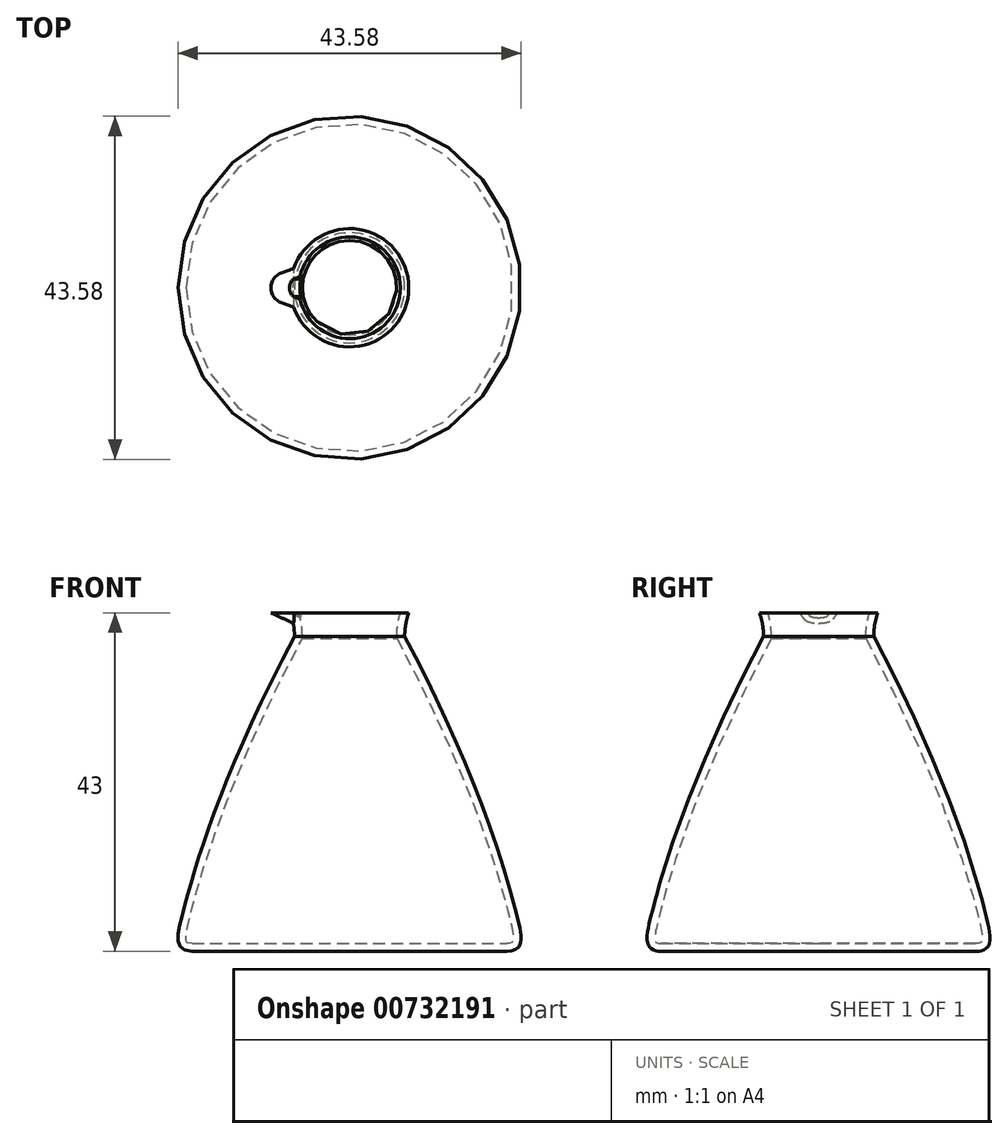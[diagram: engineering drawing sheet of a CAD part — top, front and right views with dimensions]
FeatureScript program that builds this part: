
annotation { "Feature Type Name" : "Feature", "Feature Type Description" : "" }
export const myFeature = defineFeature(function(context is Context, id is Id, definition is map)
    precondition{}
    {
        {
            var Q0;
            Q0=qCreatedBy(makeId("Front.planeOp"),FACE);
            var sketch = newSketch(context, id + "F0", { "sketchPlane" : qUnion([Q0])});
            skLineSegment(sketch, "E0", {"start": v(20, 0) * mm, "end": v(0, 0) * mm});
            skLineSegment(sketch, "E1", {"start": v(0, 0) * mm, "end": v(0, 40) * mm});
            skLineSegment(sketch, "E2", {"start": v(0, 40) * mm, "end": v(7, 40) * mm});
            skFitSpline(sketch, "E3", {"points": [v(20, 0) * mm, v(21.34, 4.28) * mm, v(7, 40) * mm], "startDerivative": vector(27.3, 0.2) * mm, "endDerivative": vector(-36.03, 68.06) * mm});
            skSolve(sketch);
        }
        {
            var Q0;
            Q0 = qSketchRegion(id + "F0", true);
            var Q1;
            Q1=sQuery(id+"F0.wireOp",EDGE,"E1");
            revolve(context, id + "F1", {"surfaceOperationType" : NewSurfaceOperationType.NEW, "entities" : qUnion([Q0]), "axis" : qUnion([Q1]), "revolveType" : RevolveType.FULL});
        }
        {
            var Q0;
            Q0=qCreatedBy(makeId("Front.planeOp"),FACE);
            var sketch = newSketch(context, id + "F2", { "sketchPlane" : qUnion([Q0])});
            skLineSegment(sketch, "E4", {"start": v(7, 40) * mm, "end": v(0, 40) * mm});
            skLineSegment(sketch, "E5", {"start": v(0, 40) * mm, "end": v(0, 43) * mm});
            skLineSegment(sketch, "E6", {"start": v(0, 43) * mm, "end": v(7.51, 43) * mm});
            skArc(sketch, "E7", {"start": v(7, 40) * mm, "mid": v(7.13, 41.52) * mm, "end": v(7.51, 43) * mm});
            skSolve(sketch);
        }
        {
            var Q0;
            Q0 = qSketchRegion(id + "F2", true);
            var Q1;
            Q1=sQuery(id+"F2.wireOp",EDGE,"E5");
            revolve(context, id + "F3", {"operationType" : NewBodyOperationType.ADD, "surfaceOperationType" : NewSurfaceOperationType.NEW, "entities" : qUnion([Q0]), "axis" : qUnion([Q1]), "revolveType" : RevolveType.FULL});
        }
        {
            var Q0;
            Q0=makeQuery(id+"F3.opRevolve","SWEPT_FACE",FACE,{"disambiguationData":[OSD([sQuery(id+"F2.wireOp",EDGE,"E6")])]});
            var sketch = newSketch(context, id + "F4", { "sketchPlane" : qUnion([Q0])});
            skArc(sketch, "E8", {"start": v(-10, 0) * mm, "mid": v(-9.64, -1.15) * mm, "end": v(-8.68, -1.88) * mm});
            skLineSegment(sketch, "E9", {"start": v(0, 0) * mm, "end": v(0, -5) * mm});
            skLineSegment(sketch, "E10", {"start": v(0, -5) * mm, "end": v(-8.68, -1.88) * mm});
            skArc(sketch, "E11.MirrorCS", {"start": v(-10, 0) * mm, "mid": v(-9.64, 1.15) * mm, "end": v(-8.68, 1.88) * mm});
            skLineSegment(sketch, "E12.MirrorCS", {"start": v(0, 5) * mm, "end": v(-8.68, 1.88) * mm});
            skLineSegment(sketch, "E13.MirrorCS", {"start": v(0, 0) * mm, "end": v(0, 5) * mm});
            skSolve(sketch);
        }
        {
            var Q0;
            Q0=qCreatedBy(makeId("Front.planeOp"),FACE);
            var sketch = newSketch(context, id + "F5", { "sketchPlane" : qUnion([Q0])});
            skLineSegment(sketch, "E14", {"start": v(4.53, 40.89) * mm, "end": v(0, 43) * mm});
            skSolve(sketch);
        }
        {
            var Q0;
            Q0 = qSketchRegion(id + "F4", true);
            var Q1;
            Q1 = qConstructionFilter(qBodyType(qCreatedBy(id + "F5" ,EDGE), BodyType.WIRE), ConstructionObject.NO);
            sweep(context, id + "F6", {"operationType" : NewBodyOperationType.ADD, "profiles" : qUnion([Q0]), "path" : qUnion([Q1])});
        }
        {
            var Q0;
            Q0=makeQuery(id+"F6.boolean.opBoolean","MERGE",FACE,{"derivedFrom":[makeQuery(id+"F3.opRevolve","SWEPT_FACE",FACE,{"disambiguationData":[OSD([sQuery(id+"F2.wireOp",EDGE,"E6")])]}),makeQuery(id+"F6.opSweep","CAP_FACE",FACE,{"disambiguationData":[OSD([sQuery(id+"F4.wireOp",EDGE,"E8"),sQuery(id+"F4.wireOp",EDGE,"E9"),sQuery(id+"F4.wireOp",EDGE,"E10"),sQuery(id+"F4.wireOp",EDGE,"E11.MirrorCS"),sQuery(id+"F4.wireOp",EDGE,"E12.MirrorCS"),sQuery(id+"F4.wireOp",EDGE,"E13.MirrorCS"),sQuery(id+"F5.wireOp",VERTEX,"E14.end")])],"isStart":true})]});
            shell(context, id + "F7", {"entities" : qUnion([Q0]), "thickness" : 1 * mm});
        }
    });
